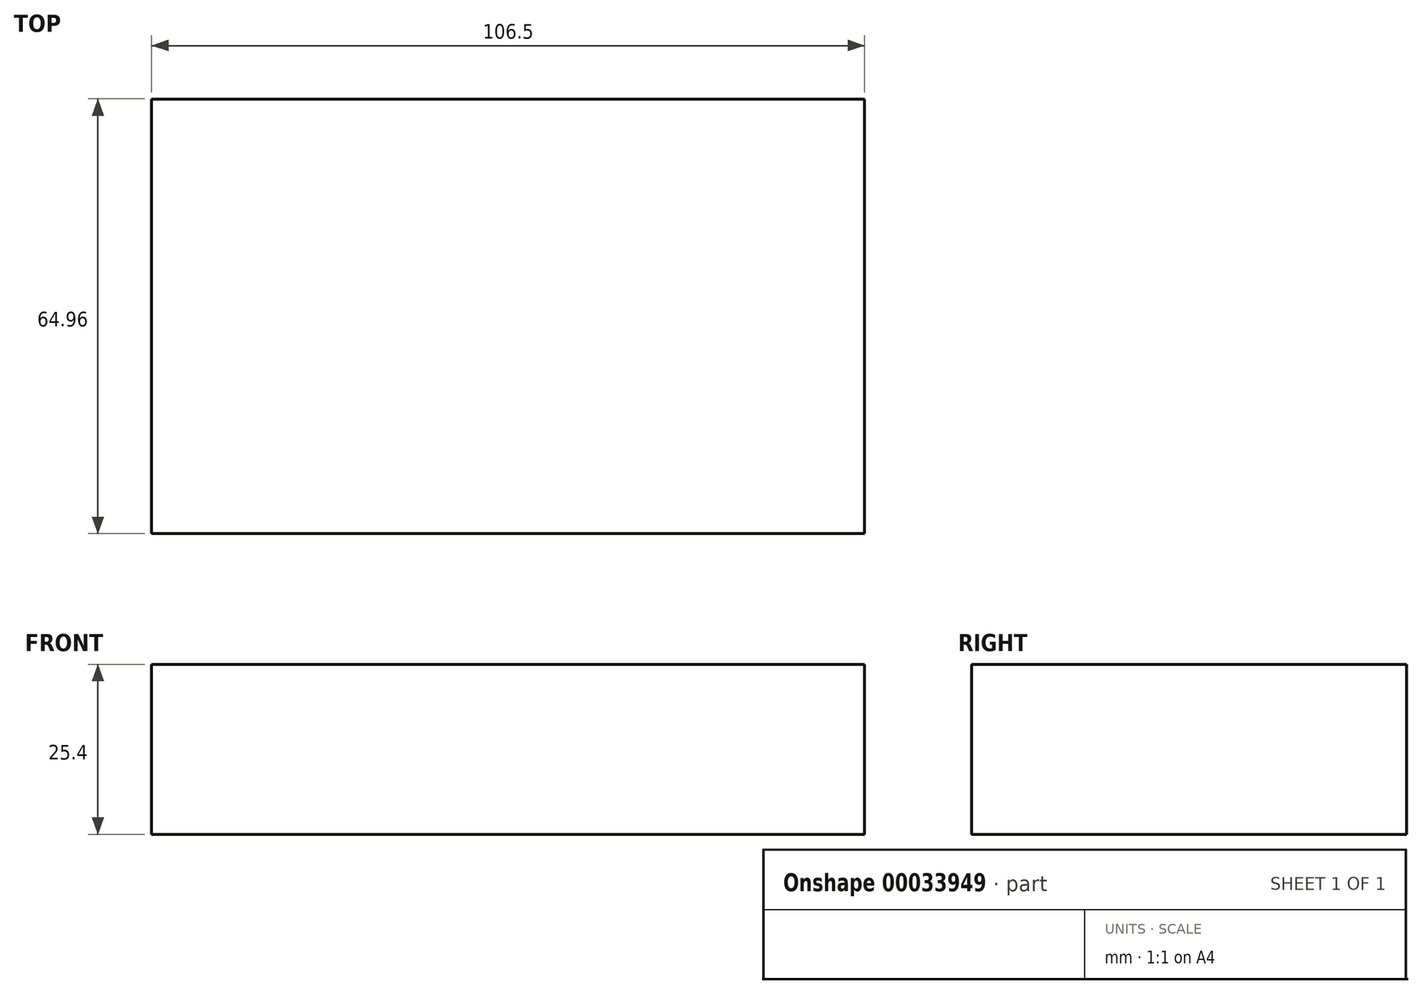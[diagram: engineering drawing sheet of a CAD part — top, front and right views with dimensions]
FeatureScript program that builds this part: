
annotation { "Feature Type Name" : "Feature", "Feature Type Description" : "" }
export const myFeature = defineFeature(function(context is Context, id is Id, definition is map)
    precondition{}
    {
        {
            var Q0;
            Q0=qCreatedBy(makeId("Top.planeOp"),FACE);
            var sketch = newSketch(context, id + "F0", { "sketchPlane" : qUnion([Q0])});
            skLineSegment(sketch, "E0.rect.bottom", {"start": v(53.25, -32.48) * mm, "end": v(-53.25, -32.48) * mm});
            skLineSegment(sketch, "E0.rect.top", {"start": v(53.25, 32.48) * mm, "end": v(-53.25, 32.48) * mm});
            skLineSegment(sketch, "E0.rect.left", {"start": v(53.25, -32.48) * mm, "end": v(53.25, 32.48) * mm});
            skLineSegment(sketch, "E0.rect.right", {"start": v(-53.25, -32.48) * mm, "end": v(-53.25, 32.48) * mm});
            skPoint(sketch, "E0.rect.middle", {"position": v(0, 0) * mm});
            skSolve(sketch);
        }
        {
            var Q0;
            Q0 = qSketchRegion(id + "F0", true);
            extrude(context, id + "F1", {"entities" : qUnion([Q0]), "depth" : 25.4 * mm});
        }
    });
